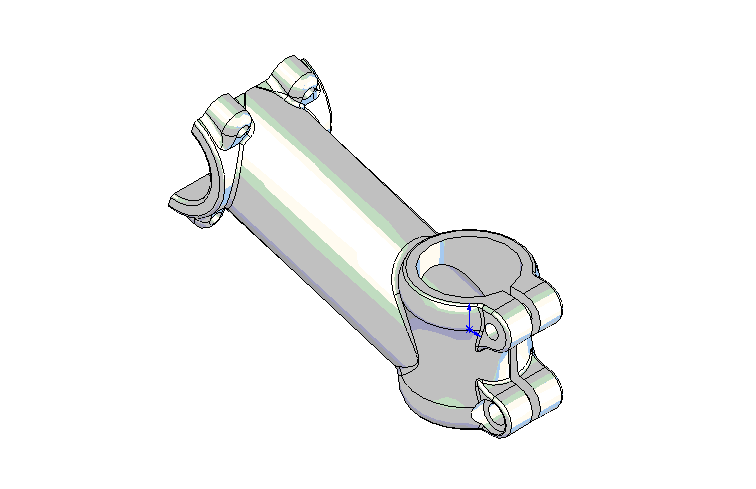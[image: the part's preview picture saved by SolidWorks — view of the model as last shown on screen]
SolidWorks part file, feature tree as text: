
SOLIDWORKS PART (.sldprt)
format: sldprt  version: not decoded by parser v0  size: 1,525,248 bytes
history: native  units: mm
features: sketch x14, cut_extrude x9, fillet x6, plane x5, extrude x4, material x1, revolve x1 (+10 scaffold rows collapsed)
feature tree (50):
  scaffold x10  (default folders/planes/origin — collapsed)
  material  "Matériau <non spécifié>"
  plane  "Plan de face"
  plane  "Plan de dessus"
  plane  "Plan de droite"
  sketch  "Esquisse1"  dims[c1.D2=~9.116966mm c1.D4=40.0mm c1.D1=41.0mm c2.D2=33.0mm c2.D3=38.0mm c2.D5=31.0mm]
  revolve  "Révolution1"  Angle=360deg
  sketch  "Esquisse4"  dims[c1.D2=13.0mm c1.D4=8.0mm c1.D3=~7.672915mm c1.D1=19.0mm c2.D3=~9.680476mm c3.D3=72.0deg c3.D4=~15.673299mm c4.D3=24.0mm]
  extrude  "Extrusion2"  Depth=21mm
  fillet  "Congé2"  Radius=1mm
  plane  "Plan1"
  plane  "Plan2"  Offset=90mm
  sketch  "Esquisse6"  dims[c1.D1=32.0mm c1.D2=4.0mm c2.D1=6.0mm c2.D2=33.0mm c2.D3=35.0mm]
  extrude  "Extrusion4"  [1 undecoded]
  sketch  "Esquisse7"  dims[D2=35.0mm D1=2.0mm]
  extrude  "Extrusion5"  Depth=42mm
  sketch  "Esquisse8"  dims[c1.D1=10.0mm c1.D2=10.0mm c1.D3=10.0mm c2.D2=25.0mm c2.D3=35.0mm]
  extrude  "Extrusion6"  Depth=10mm
  sketch  "Esquisse9"  dims[D2=28.5mm D1=3.0mm]
  cut_extrude  "Enlèv. mat.-Extru.2"  [1 undecoded]
  sketch  "Esquisse10"  dims[D1=27.0mm D2=29.0mm]
  cut_extrude  "Enlèv. mat.-Extru.3"  [1 undecoded]
  sketch  "Esquisse11"  dims[D1=25.0mm]
  cut_extrude  "Enlèv. mat.-Extru.4"  [1 undecoded]
  fillet  "Congé3"  Radius=3mm
  fillet  "Congé7"  Radius=2mm
  fillet  "Congé8"  Radius=1mm
  fillet  "Congé11"  Radius=3mm
  fillet  "Congé12"  Radius=1mm
  sketch  "Esquisse12"  dims[D1=4.2mm]
  cut_extrude  "Enlèv. mat.-Extru.6"  [1 undecoded]
  sketch  "Esquisse13"  dims[D1=5.0mm D2=~58.873673mm]
  cut_extrude  "Enlèv. mat.-Extru.7"  [1 undecoded]
  sketch  "Esquisse14"  dims[D1=6.5mm]
  cut_extrude  "Enlèv. mat.-Extru.8"  [1 undecoded]
  sketch  "Esquisse15"  dims[D1=6.5mm]
  cut_extrude  "Enlèv. mat.-Extru.9"  [1 undecoded]
  sketch  "Esquisse16"  dims[D1=10.5mm]
  cut_extrude  "Enlèv. mat.-Extru.10"  [1 undecoded]
  sketch  "Esquisse17"
  cut_extrude  "Enlèv. mat.-Extru.11"  [1 undecoded]
decode coverage: 23 of 34 modeling features carry decoded parameters
note: ~ marks probable driven/reference dimensions
note: 10 parameter values undecoded
summary: no parameter record found for 10 features
note: suppression state not decoded; provenance and decode notes live in map.json
